# Revit family: Zumtobel SLOTLIGHT INF II MSC CL
name_source: partatom
category: Lighting Fixtures
revit_build: Autodesk Revit 2018 (Build: 20170223_1515(x64)
units: mm (PartAtom-declared; Revit-internal decimal feet)

## family parameters
Cut with Voids When Loaded = No
Host = Face
Light Source = Yes
OmniClass Number = 23.80.70.11
OmniClass Title = Luminaries for Internal Lighting
Part Type = Normal
Room Calculation Point = No
Round Connector Dimension = Use Diameter
Shared = No

## types (1)
- SLN2-B CL 1600-840 L545 PC/PCO LDE
    Apparent Load = 14 VA
    Assembly Code = D5020200
    Color Filter = 16777215
    Default Elevation = 0 mm  [stored 0 ft]
    Description = SLOTLIGHT Infinity II MSC conrer luminaire
    Dimming Lamp Color Temperature Shift = <None>
    Emit Shape Visible in Rendering = No
    Emit from Rectangle Length = 71 mm  [stored 0.23294 ft]
    Emit from Rectangle Width = 545 mm  [stored 1.78806 ft]
    Height = 92 mm  [stored 0.301837 ft]
    Lamp = LED
    Length = 545 mm  [stored 1.78806 ft]
    Manufacturer = Zumtobel Lighting
    Minicell = No
    Model = 42189246+22903548
    Photometric Web File = 42189246_(840PC-4000K-diffuse_LEO1).IES
    SLN2-B = Yes
    Tilt Angle = -90.00°
    URL = http://www.zumtobel.com
    Voltage = 230 V
    Width = 76 mm  [stored 0.249344 ft]

note: [stored X ft] marks values corroborated as IEEE doubles in the binary element streams (Revit-internal decimal feet)

## geometry (parser evidence)
native form markers: Sweep x8
no freeform markers — native parametric forms only
